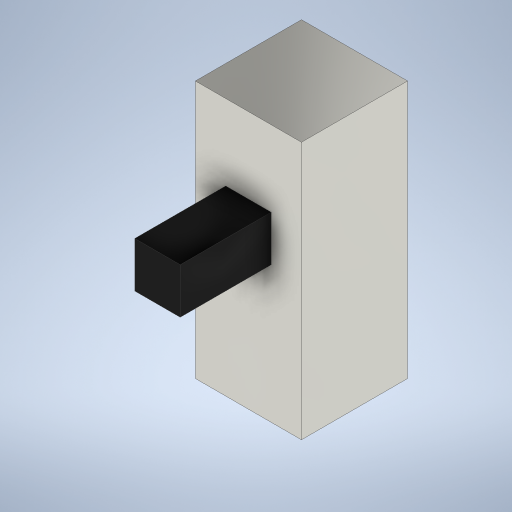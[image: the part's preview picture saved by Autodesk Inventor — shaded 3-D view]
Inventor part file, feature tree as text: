
AUTODESK INVENTOR PART (.ipt)
format: ipt  version: 2024.3 (Build 283343000, 343)  size: 239,104 bytes
history: native  units: mm
features: extrude x2, sketch x2
ambient origin geometry x8: Origin, YZ Plane, XZ Plane, XY Plane, X Axis, Y Axis, Z Axis, Center Point
bodies: Solid1 (feature_tree)
feature tree (4):
  extrude  "Extrusion1"  Depth=8.5mm
  extrude  "Extrusion2"  Depth=1.5mm
  sketch  "Sketch1"  dims[d0=3.5mm d1=8.5mm]
  sketch  "Sketch2"  dims[d2=3.5mm d3=0.0mm d4=1.5mm d5=1.5mm d6=4.0mm d7=3.0mm d8=0.0mm]
